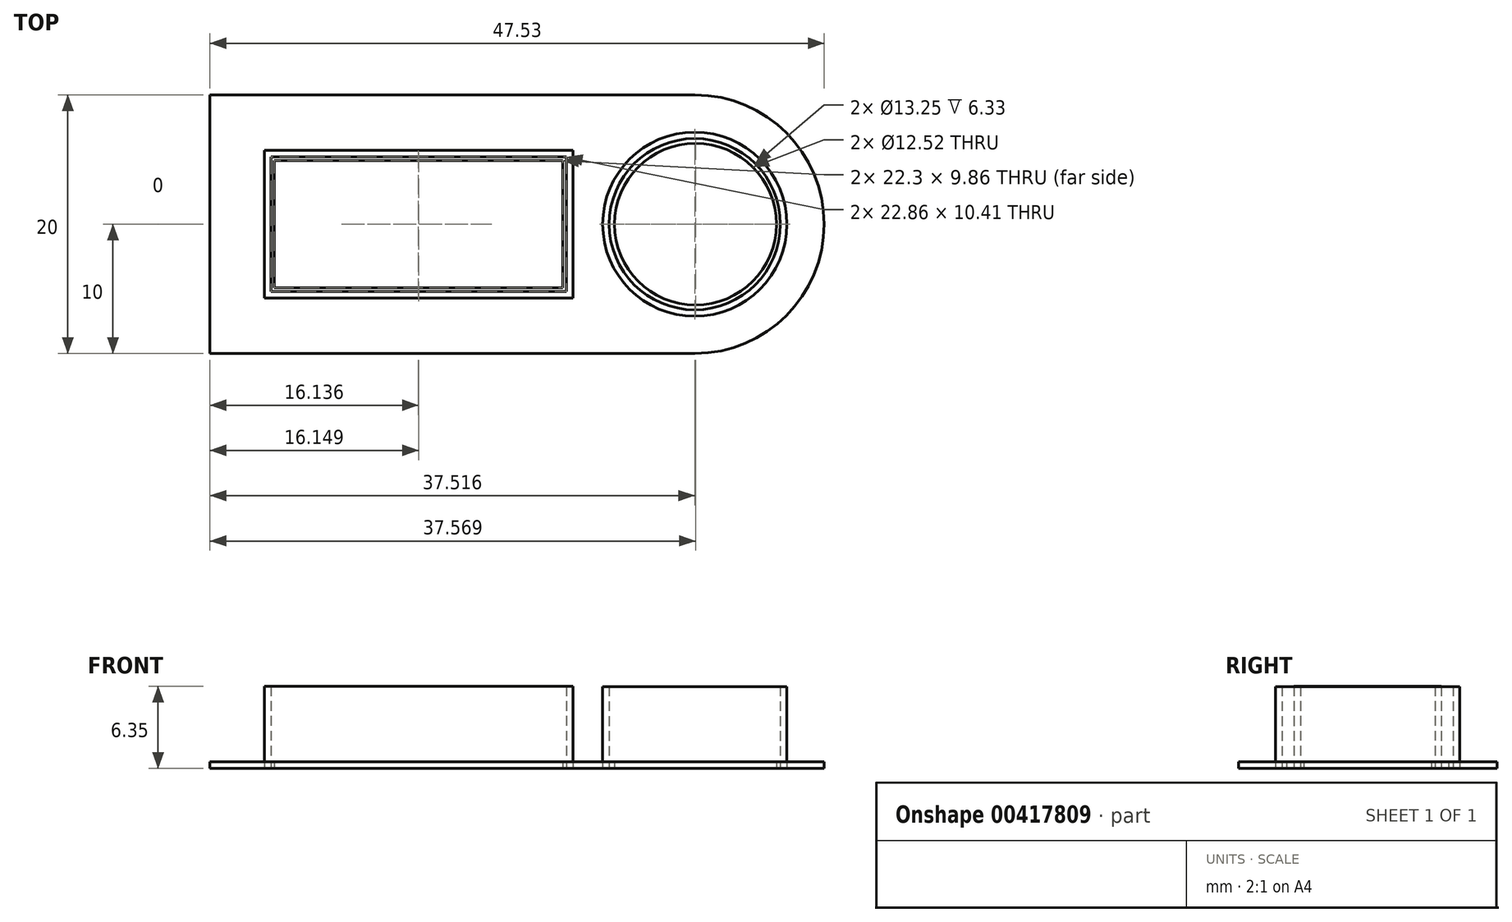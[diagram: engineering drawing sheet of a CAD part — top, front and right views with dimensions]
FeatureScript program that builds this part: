
annotation { "Feature Type Name" : "Feature", "Feature Type Description" : "" }
export const myFeature = defineFeature(function(context is Context, id is Id, definition is map)
    precondition{}
    {
        {
            var Q0;
            Q0=qCreatedBy(makeId("Top.planeOp"),FACE);
            var sketch = newSketch(context, id + "F0", { "sketchPlane" : qUnion([Q0])});
            skLineSegment(sketch, "E0.left", {"start": v(-24.5, -10) * mm, "end": v(-24.5, 10) * mm});
            skPoint(sketch, "E0.middle", {"position": v(0, 0) * mm});
            skLineSegment(sketch, "E1.bottom", {"start": v(2.79, -4.93) * mm, "end": v(-19.51, -4.93) * mm});
            skLineSegment(sketch, "E1.top", {"start": v(2.79, 4.93) * mm, "end": v(-19.51, 4.93) * mm});
            skLineSegment(sketch, "E1.left", {"start": v(2.79, -4.93) * mm, "end": v(2.79, 4.93) * mm});
            skLineSegment(sketch, "E1.right", {"start": v(-19.51, -4.93) * mm, "end": v(-19.51, 4.93) * mm});
            skPoint(sketch, "E1.middle", {"position": v(-8.36, 0) * mm});
            skCircle(sketch, "E2", {"center": v(13.07, 0) * mm, "radius": 6.26 * mm});
            skLineSegment(sketch, "E3.bottom", {"start": v(-24.5, 10) * mm, "end": v(13.03, 10) * mm});
            skLineSegment(sketch, "E3.top", {"start": v(-24.5, -10) * mm, "end": v(13.03, -10) * mm});
            skLineSegment(sketch, "E3.left", {"start": v(-24.5, 10) * mm, "end": v(-24.5, -10) * mm});
            skArc(sketch, "E4", {"start": v(13.03, 10) * mm, "mid": v(23.03, 0) * mm, "end": v(13.03, -10) * mm});
            skSolve(sketch);
        }
        {
            var Q0;
            Q0=makeQuery(id+"F0.imprint","IMPRINT",FACE,{"disambiguationData":[TD([[makeQuery(id+"F0.imprint","IMPRINT",EDGE,{"derivedFrom":sQuery(id+"F0.wireOp",EDGE,"E1.bottom")}),1.0]])]});
            extrude(context, id + "F1", {"entities" : qUnion([Q0]), "depth" : .5 * mm});
        }
        {
            var Q0;
            Q0=qCreatedBy(makeId("Top.planeOp"),FACE);
            var sketch = newSketch(context, id + "F2", { "sketchPlane" : qUnion([Q0])});
            skLineSegment(sketch, "E5.bottom", {"start": v(-23.5, 9) * mm, "end": v(23.5, 9) * mm});
            skLineSegment(sketch, "E5.top", {"start": v(-23.5, -9) * mm, "end": v(23.5, -9) * mm});
            skLineSegment(sketch, "E5.left", {"start": v(-23.5, 9) * mm, "end": v(-23.5, -9) * mm});
            skLineSegment(sketch, "E5.right", {"start": v(23.5, 9) * mm, "end": v(23.5, -9) * mm});
            skPoint(sketch, "E5.middle", {"position": v(0, 0) * mm});
            skLineSegment(sketch, "E6.bottom", {"start": v(22.5, -8) * mm, "end": v(-22.5, -8) * mm});
            skLineSegment(sketch, "E6.top", {"start": v(22.5, 8) * mm, "end": v(-22.5, 8) * mm});
            skLineSegment(sketch, "E6.left", {"start": v(22.5, -8) * mm, "end": v(22.5, 8) * mm});
            skLineSegment(sketch, "E6.right", {"start": v(-22.5, -8) * mm, "end": v(-22.5, 8) * mm});
            skSolve(sketch);
        }
        {
            var Q0;
            Q0=qCreatedBy(makeId("Top.planeOp"),FACE);
            var sketch = newSketch(context, id + "F3", { "sketchPlane" : qUnion([Q0])});
            skCircle(sketch, "E7", {"center": v(13.02, 0) * mm, "radius": 6.62 * mm});
            skCircle(sketch, "E8", {"center": v(13.02, 0) * mm, "radius": 7.12 * mm});
            skSolve(sketch);
        }
        {
            var Q0;
            Q0=makeQuery(id+"F3.imprint","IMPRINT",FACE,{"disambiguationData":[TD([[makeQuery(id+"F3.imprint","IMPRINT",EDGE,{"derivedFrom":sQuery(id+"F3.wireOp",EDGE,"E7")}),-1.0]])]});
            extrude(context, id + "F4", {"entities" : qUnion([Q0]), "depth" : 6.33 * mm});
        }
        {
            var Q0;
            Q0=qCreatedBy(makeId("Top.planeOp"),FACE);
            var sketch = newSketch(context, id + "F5", { "sketchPlane" : qUnion([Q0])});
            skLineSegment(sketch, "E9.bottom", {"start": v(3.08, -5.2) * mm, "end": v(-19.78, -5.2) * mm});
            skLineSegment(sketch, "E9.top", {"start": v(3.08, 5.2) * mm, "end": v(-19.78, 5.2) * mm});
            skLineSegment(sketch, "E9.left", {"start": v(3.08, -5.2) * mm, "end": v(3.08, 5.2) * mm});
            skLineSegment(sketch, "E9.right", {"start": v(-19.78, -5.2) * mm, "end": v(-19.78, 5.2) * mm});
            skPoint(sketch, "E9.middle", {"position": v(-8.35, 0) * mm});
            skLineSegment(sketch, "E10.bottom", {"start": v(3.58, -5.7) * mm, "end": v(-20.28, -5.7) * mm});
            skLineSegment(sketch, "E10.top", {"start": v(3.58, 5.7) * mm, "end": v(-20.28, 5.7) * mm});
            skLineSegment(sketch, "E10.left", {"start": v(3.58, -5.7) * mm, "end": v(3.58, 5.7) * mm});
            skLineSegment(sketch, "E10.right", {"start": v(-20.28, -5.7) * mm, "end": v(-20.28, 5.7) * mm});
            skSolve(sketch);
        }
        {
            var Q0;
            Q0=makeQuery(id+"F5.imprint","IMPRINT",FACE,{"disambiguationData":[TD([[makeQuery(id+"F5.imprint","IMPRINT",EDGE,{"derivedFrom":sQuery(id+"F5.wireOp",EDGE,"E9.bottom")}),1.0]])]});
            extrude(context, id + "F6", {"entities" : qUnion([Q0]), "depth" : 6.35 * mm});
        }
    });
